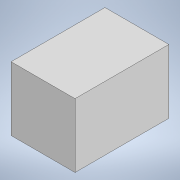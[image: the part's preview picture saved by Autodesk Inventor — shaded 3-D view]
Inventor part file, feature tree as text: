
AUTODESK INVENTOR PART (.ipt)
format: ipt  version: 2020.3 (Build 243373000, 373)  size: 105,984 bytes
history: native  units: mm
features: sketch x4, extrude x3
ambient origin geometry x8: Origin, YZ Plane, XZ Plane, XY Plane, X Axis, Y Axis, Z Axis, Center Point
bodies: Solid1 (feature_tree)
feature tree (7):
  extrude  "Extrusion1"  Depth=47.9mm
  extrude  "Extrusion2"  Depth=85.0mm TaperAngle=0.0deg
  extrude  "Extrusion3"  Depth=5.0mm
  sketch  "Sketch4"  dims[d8=8.0mm d9=0.0mm]
  sketch  "Sketch1"  dims[d0=47.9mm d1=47.9mm]
  sketch  "Sketch2"  dims[d2=5.0mm d3=85.0mm d4=0.0mm]
  sketch  "Sketch3"  dims[d5=5.0mm d6=0.0mm d7=32.0mm]
